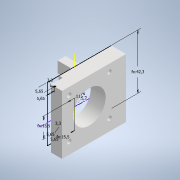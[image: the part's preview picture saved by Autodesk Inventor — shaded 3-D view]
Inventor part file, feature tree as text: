
AUTODESK INVENTOR PART (.ipt)
format: ipt  version: 2022.2 (Build 262287000, 287)  size: 2,201,600 bytes
history: native  units: mm
features: sketch x12, extrude x7, other x4, projected_geometry x3, hole x2, thread x2, revolve x2, helix x2, fillet x1, plane x1, reference x1
ambient origin geometry x8: Origin, YZ Plane, XZ Plane, XY Plane, X Axis, Y Axis, Z Axis, Center Point
bodies: Solid1 (feature_tree), Solid2 (feature_tree), Solid3 (feature_tree)
feature tree (37):
  other  "Motor.ipt"
  extrude  "Extrusion1"  Depth=10.0mm
  extrude  "Extrusion2"  Depth=3.3mm
  extrude  "Extrusion4"  Depth=15.500005mm
  extrude  "Extrusion5"  Depth=5.65mm
  fillet  "Fillet1"  Radius=11.5mm
  hole  "Hole1"  [1 undecoded]
  thread  "Thread1"  [1 undecoded]
  thread  "Thread2"  [1 undecoded]
  sketch  "Sketch8"  dims[d17=5.65mm d18=5.65mm]
  plane  "Work Plane1"
  extrude  "Extrusion6"  Depth=5.65mm
  extrude  "Extrusion7"  Depth=5.2mm
  revolve  "Revolution1"  [1 undecoded]
  helix  "Coil1"  [1 undecoded]
  revolve  "Revolution2"  [1 undecoded]
  helix  "Coil2"  [1 undecoded]
  hole  "Hole2"  [1 undecoded]
  extrude  "Extrusion8"  TaperAngle=0.0deg  [1 undecoded]
  sketch  "Sketch2"  dims[d0=10.0mm d1=11.0mm]
  sketch  "Sketch3"  dims[d2=5.7mm d3=3.3mm]
  projected_geometry  "Projected Loop1"
  sketch  "Sketch5"  dims[d4=15.500005mm d5=15.500005mm]
  sketch  "Sketch6"  dims[d6=5.65mm d7=5.65mm d8=11.5mm d9=0.0mm]
  projected_geometry  "Projected Loop2"
  sketch  "Sketch7"  dims[d10=25.0mm d11=2.4mm d12=0.0mm d15=42.3mm d16=3.3mm]
  projected_geometry  "Projected Loop4"
  reference  "Reference1"
  sketch  "Sketch10"  dims[d22=10.5mm d23=0.0mm d24=5.2mm]
  sketch  "Sketch11"  dims[d25=4.0mm d26=0.0mm d27=1.0mm]
  sketch  "Sketch12"  dims[d28=3.18mm d29=6.0mm d30=4.0mm d31=2.0mm d32=90.0deg d33=8.0mm d34=20.594885mm d35=8.0mm d36=0.0mm]
  sketch  "Sketch13"  dims[d37=8.0mm d38=0.0mm d39=5.0mm d40=0.0mm d41=3.0mm d42=0.0mm]
  sketch  "Sketch14"  dims[d43=9.599311mm d44=0.080042mm d45=0.080042mm d48=0.5mm]
  sketch  "Sketch15"  dims[d50=9.599311mm d52=0.0mm d53=0.5005mm d54=9.0mm d55=10.0mm d56=0.0mm d57=0.0mm d58=0.0mm d59=0.0mm d60=0.0mm d61=9.599311mm d62=0.080042mm d63=0.080042mm d66=0.5mm d68=9.599311mm d70=0.0mm d71=0.5005mm d72=9.0mm d73=10.0mm d74=0.0mm d75=0.0mm d76=0.0mm d77=0.0mm d78=0.0mm d79=31.000011mm d80=31.000011mm d81=3.18mm d82=6.0mm d83=6.0mm d84=4.0mm d85=90.0deg d86=8.0mm d87=20.594885mm d88=8.0mm d89=3.0mm d90=0.0mm d91=17.0mm d92=6.0mm]
  other  "<userpath>\Documents\Inventor\Wire Bender\Assembly.iam"
  other  "Assembly.iam"
  other  "Bending Base:1"
note: 9 required parameter values undecoded (feature->parameter linkage not recoverable at this tier; creation-order binding heuristic only, values carry confidence <= 0.55)